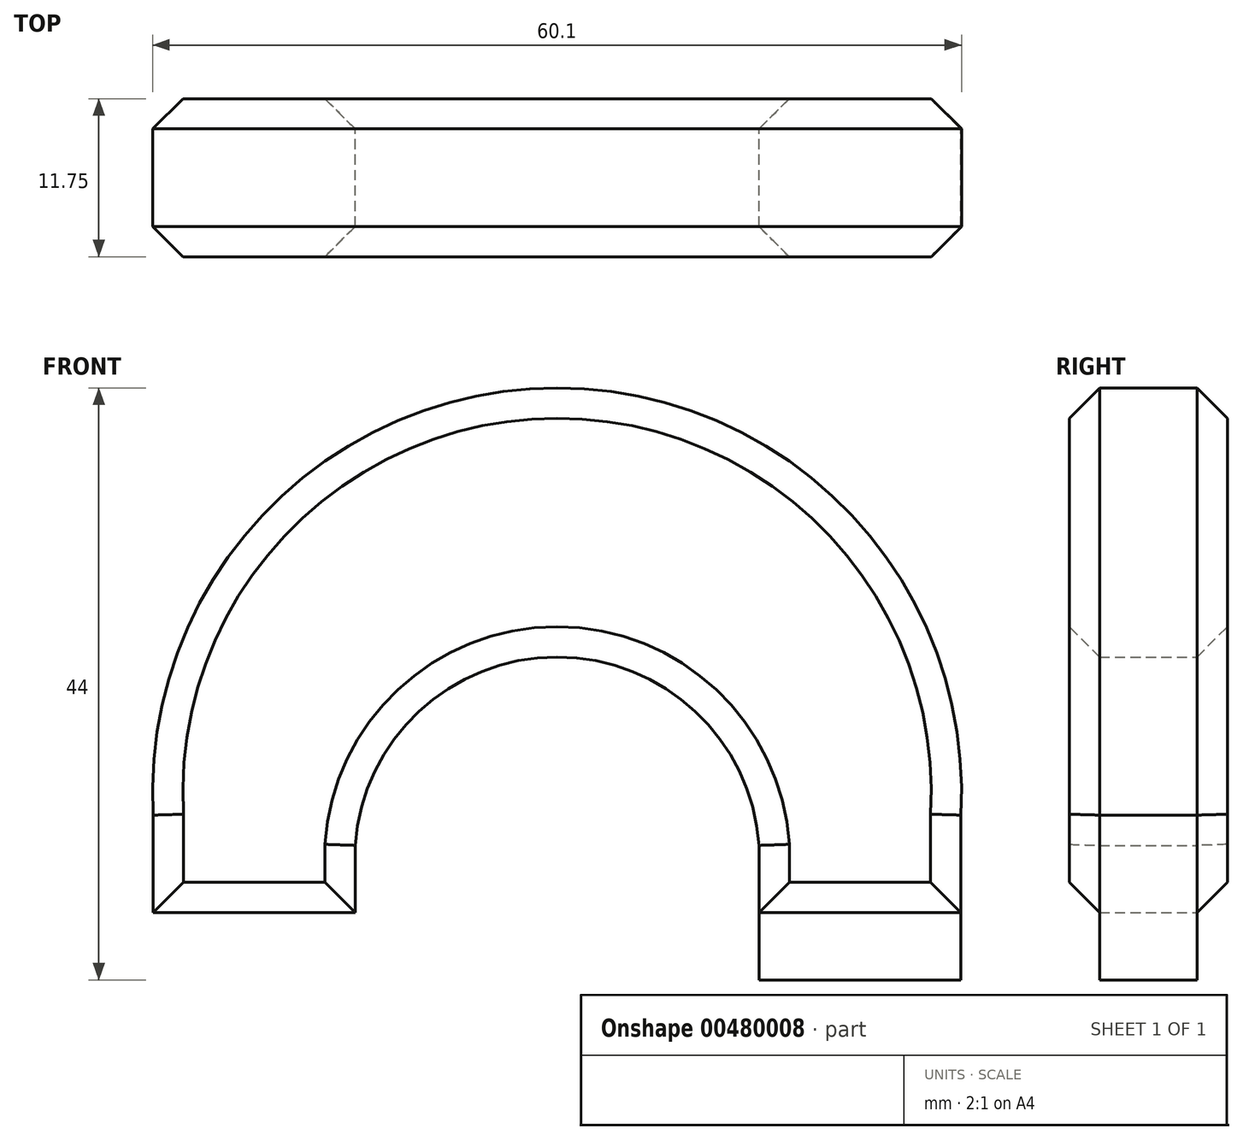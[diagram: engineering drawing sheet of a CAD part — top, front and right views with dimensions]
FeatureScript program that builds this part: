
annotation { "Feature Type Name" : "Feature", "Feature Type Description" : "" }
export const myFeature = defineFeature(function(context is Context, id is Id, definition is map)
    precondition{}
    {
        {
            var Q0;
            Q0=qCreatedBy(makeId("Front.planeOp"),FACE);
            var sketch = newSketch(context, id + "F0", { "sketchPlane" : qUnion([Q0])});
            skLineSegment(sketch, "E0", {"start": v(-30, 0) * mm, "end": v(-45, 0) * mm});
            skLineSegment(sketch, "E1", {"start": v(0, 0) * mm, "end": v(15, 0) * mm});
            skLineSegment(sketch, "E2", {"start": v(-30, 0) * mm, "end": v(-30, 5) * mm});
            skLineSegment(sketch, "E3", {"start": v(0, 0) * mm, "end": v(0, 5) * mm});
            skPoint(sketch, "E4", {"position": v(-15, 19) * mm});
            skArc(sketch, "E5", {"start": v(0, 5) * mm, "mid": v(-15, 19) * mm, "end": v(-30, 5) * mm});
            skLineSegment(sketch, "E6", {"start": v(-45, 0) * mm, "end": v(-45, 7.25) * mm});
            skLineSegment(sketch, "E7", {"start": v(15, 0) * mm, "end": v(15, 7.25) * mm});
            skPoint(sketch, "E8", {"position": v(-15, 39) * mm});
            skArc(sketch, "E9", {"start": v(15, 7.25) * mm, "mid": v(-15, 39) * mm, "end": v(-45, 7.25) * mm});
            skSolve(sketch);
        }
        {
            var Q0;
            Q0=makeQuery(id+"F0.imprint","IMPRINT",FACE,{"disambiguationData":[TD([[makeQuery(id+"F0.imprint","IMPRINT",EDGE,{"derivedFrom":sQuery(id+"F0.wireOp",EDGE,"E0")}),-1.0]])]});
            extrude(context, id + "F1", {"entities" : qUnion([Q0]), "depth" : 7.25 * mm});
        }
        {
            var Q0;
            Q0=makeQuery(id+"F1.opExtrude","CAP_FACE",FACE,{"disambiguationData":[OSD([sQuery(id+"F0.wireOp",EDGE,"E0"),sQuery(id+"F0.wireOp",EDGE,"E1"),sQuery(id+"F0.wireOp",EDGE,"E2"),sQuery(id+"F0.wireOp",EDGE,"E3"),sQuery(id+"F0.wireOp",EDGE,"E5"),sQuery(id+"F0.wireOp",EDGE,"E6"),sQuery(id+"F0.wireOp",EDGE,"E7"),sQuery(id+"F0.wireOp",EDGE,"E9")])],"isStart":false});
            var sketch = newSketch(context, id + "F2", { "sketchPlane" : qUnion([Q0])});
            skSolve(sketch);
        }
        {
            var Q0;
            Q0=makeQuery(id+"F2.imprint","IMPRINT",FACE,{"disambiguationData":[TD([[makeQuery(id+"F2.imprint","IMPRINT",EDGE,{"derivedFrom":makeQuery(id+"F1.opExtrude","CAP_EDGE",EDGE,{"disambiguationData":[OSD([sQuery(id+"F0.wireOp",EDGE,"E0")])],"isStart":false})}),-1.0]])]});
            extrude(context, id + "F3", {"entities" : qUnion([Q0]), "operationType" : NewBodyOperationType.ADD, "depth" : 2.25 * mm, "hasDraft" : true, "draftAngle" : 45 * degree, "draftPullDirection" : true});
        }
        {
            var Q0;
            Q0=makeQuery(id+"F1.opExtrude","CAP_FACE",FACE,{"disambiguationData":[OSD([sQuery(id+"F0.wireOp",EDGE,"E0"),sQuery(id+"F0.wireOp",EDGE,"E1"),sQuery(id+"F0.wireOp",EDGE,"E2"),sQuery(id+"F0.wireOp",EDGE,"E3"),sQuery(id+"F0.wireOp",EDGE,"E5"),sQuery(id+"F0.wireOp",EDGE,"E6"),sQuery(id+"F0.wireOp",EDGE,"E7"),sQuery(id+"F0.wireOp",EDGE,"E9")])],"isStart":true});
            extrude(context, id + "F4", {"entities" : qUnion([Q0]), "operationType" : NewBodyOperationType.ADD, "depth" : 2.25 * mm, "hasDraft" : true, "draftAngle" : 45 * degree, "draftPullDirection" : true});
        }
        {
            var Q0;
            Q0=makeQuery(id+"F1.opExtrude","SWEPT_FACE",FACE,{"disambiguationData":[OSD([sQuery(id+"F0.wireOp",EDGE,"E1")])]});
            extrude(context, id + "F5", {"entities" : qUnion([Q0]), "operationType" : NewBodyOperationType.ADD, "depth" : 5 * mm});
        }
    });
